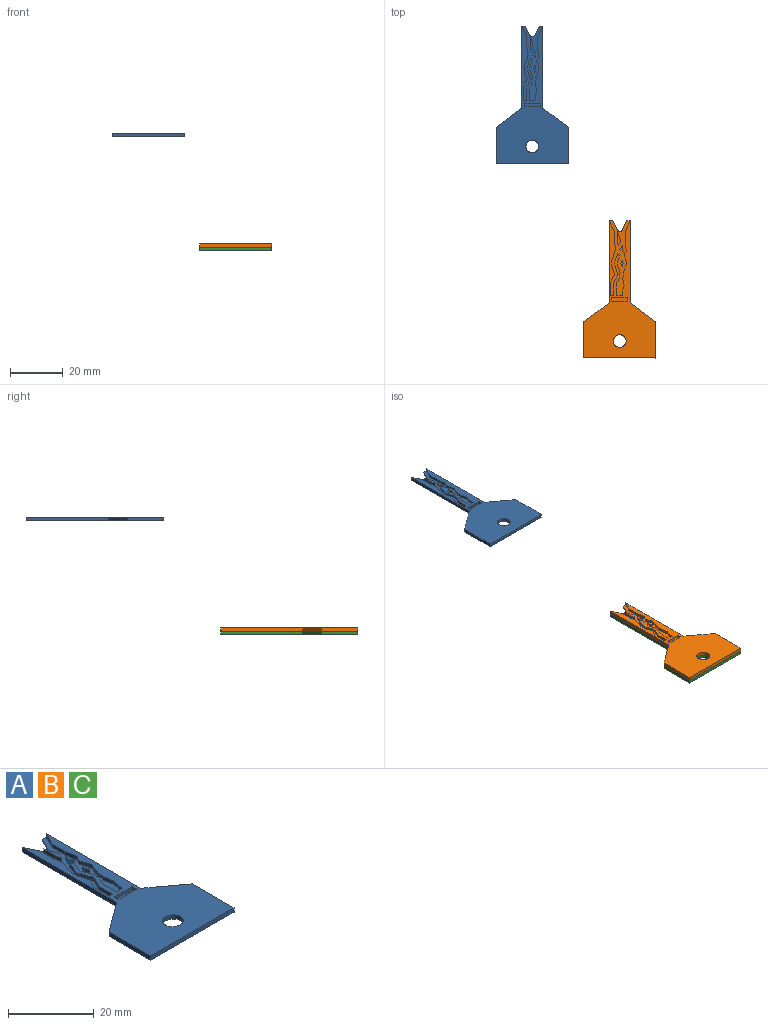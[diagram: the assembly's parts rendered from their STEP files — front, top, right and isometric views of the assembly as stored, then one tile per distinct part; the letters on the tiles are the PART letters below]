
ASSEMBLY  parts=3 mates=1
PART A: 79 faces, bbox 27.5x52.2x1.3 mm
  f0: plane 3.46x1.73mm, normal (-0.89,0.45,0), area 1mm2, adj f1,f5,f14,f75
  f1: cylinder r=1.04mm len=1.86mm, axis (0,0,1), area 0.6mm2, adj f0,f2,f14,f75
  f2: plane 3.46x1.73mm, normal (0.89,0.45,0), area 1mm2, adj f1,f6,f14,f75
  f3: plane 52.19x27.51mm, normal (0,0,1), area 615.2mm2, adj f4,f7,f8,f9,f10,f11,f12,f13
  f4: plane 31.24x1.25mm, normal (1,0,0), area 39mm2, adj f3,f5,f12,f14,f63,f75
  f5: plane 1.33x0.25mm, normal (0,1,0), area 0.3mm2, adj f0,f4,f14,f75
  f6: plane 1.34x0.25mm, normal (0,1,0), area 0.3mm2, adj f2,f7,f14,f75
  f7: plane 31.24x1.25mm, normal (-1,0,0), area 39.1mm2, adj f3,f6,f8,f14,f24
  f8: plane 9.75x7.23mm, normal (-0.6,0.8,0), area 15.2mm2, adj f3,f7,f9,f14
  f9: plane 13.72x1.25mm, normal (-1,0,0), area 17.2mm2, adj f3,f8,f10,f14
  f10: plane 27.51x1.25mm, normal (0,-1,0), area 34.4mm2, adj f3,f9,f11,f14
  f11: plane 13.72x1.25mm, normal (1,0,0), area 17.2mm2, adj f3,f10,f12,f14
  f12: plane 9.75x7.23mm, normal (0.6,0.8,0), area 15.2mm2, adj f3,f4,f11,f14
  f13: cylinder r=2.42mm len=4.83mm, axis (0,0,1), area 19mm2, adj f3,f14
  f14: plane 52.19x27.51mm, normal (0,0,-1), area 724.2mm2, adj f0,f1,f2,f4,f5,f6,f7,f8
  f15: plane 1.1x1mm, normal (-1,0,0), area 1.1mm2, adj f3,f16,f22,f23
  f16: cylinder r=0.2mm len=1mm, axis (0,0,1), area 0.3mm2, adj f3,f15,f17,f23
  f17: plane 5.6x1mm, normal (0,-1,0), area 5.6mm2, adj f3,f16,f18,f23
  f18: cylinder r=0.2mm len=1mm, axis (0,0,1), area 0.3mm2, adj f3,f17,f19,f23
  f19: plane 1.1x1mm, normal (1,0,0), area 1.1mm2, adj f3,f18,f20,f23
  f20: cylinder r=0.2mm len=1mm, axis (0,0,1), area 0.3mm2, adj f3,f19,f21,f23
  f21: plane 5.6x1mm, normal (0,1,0), area 5.6mm2, adj f3,f20,f22,f23
  f22: cylinder r=0.2mm len=1mm, axis (0,0,1), area 0.3mm2, adj f3,f15,f21,f23
  f23: plane 6x1.5mm, normal (0,0,1), area 9mm2, adj f15,f16,f17,f18,f19,f20,f21,f22
  f24: plane 4x2mm, normal (0.89,0.45,0), area 4.5mm2, adj f3,f7,f25,f75
  f25: plane 4x1mm, normal (1,0,0), area 4mm2, adj f3,f24,f26,f75
  f26: plane 3.05x1mm, normal (0.99,0.14,0), area 3.1mm2, adj f3,f25,f27,f75
  f27: plane 4.2x1.43mm, normal (0.95,-0.32,0), area 4.4mm2, adj f3,f26,f28,f75
  f28: plane 2x1mm, normal (1,-0.01,0), area 2mm2, adj f3,f27,f29,f75
  f29: plane 3.12x1.07mm, normal (0.95,0.32,0), area 3.3mm2, adj f3,f28,f30,f75
  f30: plane 2.93x1.56mm, normal (0.88,-0.47,0), area 3.3mm2, adj f3,f29,f31,f75
  f31: plane 5x1mm, normal (1,0,0), area 5mm2, adj f3,f30,f32,f75
  f32: plane 1.2x1mm, normal (0,1,0), area 1.2mm2, adj f3,f31,f33,f75
  f33: plane 4.7x1mm, normal (-1,0,0), area 4.7mm2, adj f3,f32,f34,f75
  f34: plane 2.66x1.42mm, normal (-0.88,0.47,0), area 3mm2, adj f3,f33,f35,f75
  f35: plane 1x0.95mm, normal (-1,0.08,0), area 1mm2, adj f3,f34,f36,f75
  f36: plane 3.12x1.07mm, normal (-0.95,-0.32,0), area 3.3mm2, adj f3,f35,f37,f75
  f37: plane 1x0.61mm, normal (-0.94,-0.35,0), area 0.7mm2, adj f3,f36,f38,f75
  f38: plane 1x0.61mm, normal (-0.93,0.37,0), area 0.7mm2, adj f3,f37,f39,f75
  f39: plane 3.25x1.11mm, normal (-0.95,0.32,0), area 3.4mm2, adj f3,f38,f40,f75
  f40: plane 1x0.87mm, normal (0.53,0.85,0), area 1mm2, adj f3,f39,f41,f75
  f41: plane 3.03x1.03mm, normal (0.95,-0.32,0), area 3.2mm2, adj f3,f40,f42,f75
  f42: plane 1x0.58mm, normal (1,-0.03,0), area 0.6mm2, adj f3,f41,f43,f75
  f43: plane 3.12x1.07mm, normal (0.95,0.32,0), area 3.3mm2, adj f3,f42,f44,f75
  f44: plane 1x0.38mm, normal (0.89,-0.46,0), area 0.4mm2, adj f3,f43,f45,f75
  f45: plane 1x0.95mm, normal (1,-0.08,0), area 1mm2, adj f3,f44,f46,f75
  f46: plane 1x0.45mm, normal (0.91,0.42,0), area 0.5mm2, adj f3,f45,f47,f75
  f47: plane 2.2x1.17mm, normal (0.88,-0.47,0), area 2.5mm2, adj f3,f46,f48,f75
  f48: plane 4.66x1mm, normal (1,0,0), area 4.7mm2, adj f3,f47,f49,f75
  f49: plane 2.12x1mm, normal (0,1,0), area 2.1mm2, adj f3,f48,f50,f75
  f50: plane 1.56x1mm, normal (-1,0.04,0), area 1.6mm2, adj f3,f49,f51,f75
  f51: plane 2.1x1mm, normal (-0.96,0.26,0), area 2.2mm2, adj f3,f50,f52,f75
  f52: plane 3.12x1mm, normal (-0.98,-0.18,0), area 3.2mm2, adj f3,f51,f53,f75
  f53: plane 1x0.41mm, normal (-0.83,0.56,0), area 0.5mm2, adj f3,f52,f54,f75
  f54: plane 1x0.95mm, normal (-1,0.08,0), area 1mm2, adj f3,f53,f55,f75
  f55: plane 1x0.41mm, normal (-0.95,-0.31,0), area 0.4mm2, adj f3,f54,f56,f75
  f56: plane 1.75x1mm, normal (-0.93,0.37,0), area 1.9mm2, adj f3,f55,f57,f75
  f57: plane 1.28x1mm, normal (-0.93,0.38,0), area 1.4mm2, adj f3,f56,f58,f75
  f58: plane 1x0.87mm, normal (-1,0,0), area 0.9mm2, adj f3,f57,f59,f75
  f59: plane 2.9x1mm, normal (-0.96,-0.29,0), area 3mm2, adj f3,f58,f60,f75
  f60: plane 1.21x1mm, normal (-0.8,0.6,0), area 1.5mm2, adj f3,f59,f61,f75
  f61: plane 3.75x1mm, normal (-0.99,-0.14,0), area 3.8mm2, adj f3,f60,f62,f75
  f62: plane 4x1mm, normal (-1,0,0), area 4mm2, adj f3,f61,f63,f75
  f63: plane 3.98x1.99mm, normal (-0.89,0.45,0), area 4.5mm2, adj f3,f4,f62,f75
  f64: plane 1.28x1mm, normal (-0.93,0.36,0), area 1.4mm2, adj f65,f72,f75,f77
  f65: plane 1.28x1mm, normal (0.93,0.38,0), area 1.4mm2, adj f64,f66,f75,f77
  f66: plane 1.28x1mm, normal (0.93,-0.38,0), area 1.4mm2, adj f65,f72,f75,f77
  f67: plane 3.92x1mm, normal (-1,0,0), area 3.9mm2, adj f68,f73,f75,f76
  f68: plane 4x1.2mm, normal (0.96,0.29,0), area 4.2mm2, adj f67,f69,f75,f76
  f69: plane 1.53x1mm, normal (0.84,-0.54,0), area 1.8mm2, adj f68,f73,f75,f76
  f70: plane 1.72x1mm, normal (-0.87,0.48,0), area 2mm2, adj f71,f74,f75,f78
  f71: plane 2.58x1mm, normal (0.99,0.14,0), area 2.6mm2, adj f70,f74,f75,f78
  f72: plane 1.28x1mm, normal (-0.93,-0.36,0), area 1.4mm2, adj f64,f66,f75,f77
  f73: plane 1.61x1mm, normal (-0.99,-0.14,0), area 1.6mm2, adj f67,f69,f75,f76
  f74: plane 1.31x1mm, normal (-0.55,-0.84,0), area 1.6mm2, adj f70,f71,f75,f78
  f75: plane 28.3x8mm, normal (0,0,1), area 93.9mm2, adj f0,f1,f2,f4,f5,f6,f24,f25
  f76: plane 5.53x1.2mm, normal (0,0,1), area 3.3mm2, adj f67,f68,f69,f73
  f77: plane 2.56x1.03mm, normal (0,0,1), area 1.3mm2, adj f64,f65,f66,f72
  f78: plane 2.58x1.31mm, normal (0,0,1), area 1.5mm2, adj f70,f71,f74
PART B: same geometry as A
PART C: same geometry as A
PLACE A t=(22.32,79.42,8.6)mm
PLACE B t=(55.6,5.43,-33.39)mm
PLACE C rot(axis=(0,-1,0),180deg) t=(54.6,5.43,-35.89)mm
MATE fastened C.f13 <-> B.f13  axis (0,0,1) through (55.1,-8.9,-34.64)mm
